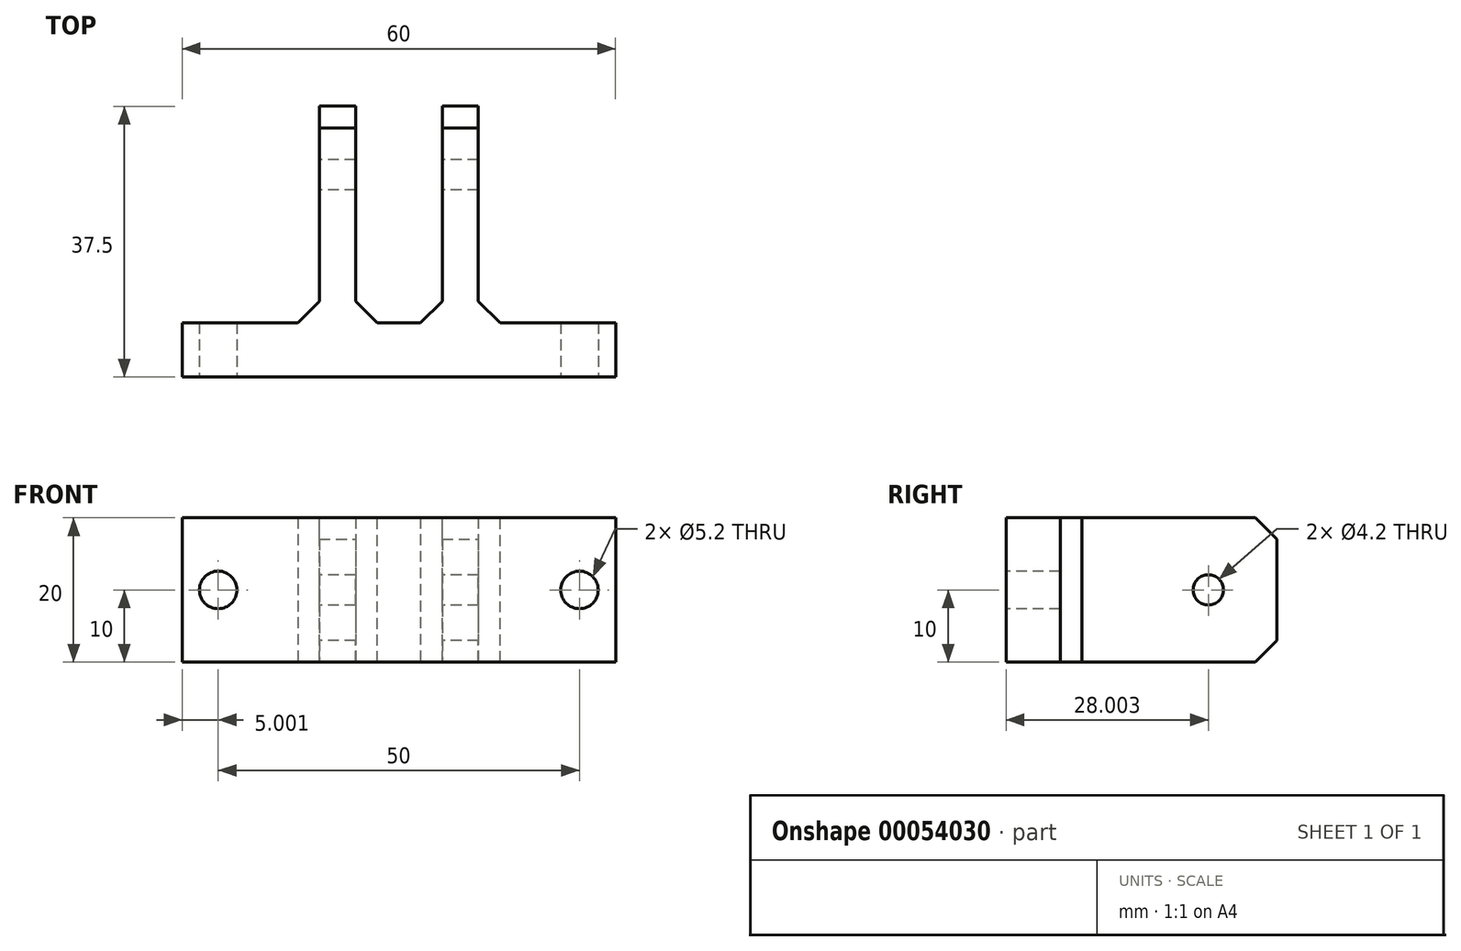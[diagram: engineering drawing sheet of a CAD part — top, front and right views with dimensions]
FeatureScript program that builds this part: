
annotation { "Feature Type Name" : "Feature", "Feature Type Description" : "" }
export const myFeature = defineFeature(function(context is Context, id is Id, definition is map)
    precondition{}
    {
        {
            var Q0;
            Q0=qCreatedBy(makeId("Top.planeOp"),FACE);
            var sketch = newSketch(context, id + "F0", { "sketchPlane" : qUnion([Q0])});
            skLineSegment(sketch, "E0.bottom", {"start": v(6.11, 32.08) * mm, "end": v(66.11, 32.08) * mm});
            skLineSegment(sketch, "E0.top", {"start": v(6.11, 39.58) * mm, "end": v(66.11, 39.58) * mm});
            skLineSegment(sketch, "E0.left", {"start": v(6.11, 32.08) * mm, "end": v(6.11, 39.58) * mm});
            skLineSegment(sketch, "E0.right", {"start": v(66.11, 32.08) * mm, "end": v(66.11, 39.58) * mm});
            skLineSegment(sketch, "E1.bottom", {"start": v(25.11, 39.58) * mm, "end": v(30.11, 39.58) * mm});
            skLineSegment(sketch, "E1.top", {"start": v(25.11, 69.58) * mm, "end": v(30.11, 69.58) * mm});
            skLineSegment(sketch, "E1.left", {"start": v(25.11, 39.58) * mm, "end": v(25.11, 69.58) * mm});
            skLineSegment(sketch, "E1.right", {"start": v(30.11, 39.58) * mm, "end": v(30.11, 69.58) * mm});
            skLineSegment(sketch, "E2.bottom", {"start": v(42.11, 69.58) * mm, "end": v(47.11, 69.58) * mm});
            skLineSegment(sketch, "E2.top", {"start": v(42.11, 39.58) * mm, "end": v(47.11, 39.58) * mm});
            skLineSegment(sketch, "E2.left", {"start": v(42.11, 69.58) * mm, "end": v(42.11, 39.58) * mm});
            skLineSegment(sketch, "E2.right", {"start": v(47.11, 69.58) * mm, "end": v(47.11, 39.58) * mm});
            skSolve(sketch);
        }
        {
            var Q0;
            Q0 = qSketchRegion(id + "F0", true);
            extrude(context, id + "F1", {"entities" : qUnion([Q0]), "depth" : 20 * mm});
        }
        {
            var Q0;
            Q0=makeQuery(id+"F1.opExtrude","SWEPT_FACE",FACE,{"disambiguationData":[OSD([sQuery(id+"F0.wireOp",EDGE,"E0.bottom")])]});
            var sketch = newSketch(context, id + "F2", { "sketchPlane" : qUnion([Q0])});
            skPoint(sketch, "E3", {"position": v(11.11, 10) * mm});
            skPoint(sketch, "E4", {"position": v(61.11, 10) * mm});
            skSolve(sketch);
        }
        {
            var Q0;
            Q0=sQuery(id+"F2.wireOp",VERTEX,"E3");
            var Q1;
            Q1=sQuery(id+"F2.wireOp",VERTEX,"E4");
            var Q2;
            Q2=makeQuery(id+"F1.opExtrude","SWEPT_BODY",BODY,{"disambiguationData":[OSD([sQuery(id+"F0.wireOp",EDGE,"E0.bottom"),sQuery(id+"F0.wireOp",EDGE,"E0.top"),sQuery(id+"F0.wireOp",EDGE,"E0.left"),sQuery(id+"F0.wireOp",EDGE,"E0.right"),sQuery(id+"F0.wireOp",EDGE,"E1.top"),sQuery(id+"F0.wireOp",EDGE,"E1.left"),sQuery(id+"F0.wireOp",EDGE,"E1.right"),sQuery(id+"F0.wireOp",EDGE,"E2.bottom"),sQuery(id+"F0.wireOp",EDGE,"E2.left"),sQuery(id+"F0.wireOp",EDGE,"E2.right")])]});
            hole(context, id + "F3", {"style" : HoleStyle.SIMPLE, "holeDiameter" : 5.2 * mm, "endStyle" : HoleEndStyle.THROUGH, "locations" : qUnion([Q0, Q1]), "scope" : qUnion([Q2])});
        }
        {
            var Q0;
            Q0=makeQuery(id+"F1.opExtrude","SWEPT_FACE",FACE,{"disambiguationData":[OSD([sQuery(id+"F0.wireOp",EDGE,"E1.left")])]});
            var sketch = newSketch(context, id + "F4", { "sketchPlane" : qUnion([Q0])});
            skPoint(sketch, "E5", {"position": v(-60.08, 10) * mm});
            skSolve(sketch);
        }
        {
            var Q0;
            Q0=sQuery(id+"F4.wireOp",VERTEX,"E5");
            var Q1;
            Q1=makeQuery(id+"F1.opExtrude","SWEPT_BODY",BODY,{"disambiguationData":[OSD([sQuery(id+"F0.wireOp",EDGE,"E0.bottom"),sQuery(id+"F0.wireOp",EDGE,"E0.top"),sQuery(id+"F0.wireOp",EDGE,"E0.left"),sQuery(id+"F0.wireOp",EDGE,"E0.right"),sQuery(id+"F0.wireOp",EDGE,"E1.top"),sQuery(id+"F0.wireOp",EDGE,"E1.left"),sQuery(id+"F0.wireOp",EDGE,"E1.right"),sQuery(id+"F0.wireOp",EDGE,"E2.bottom"),sQuery(id+"F0.wireOp",EDGE,"E2.left"),sQuery(id+"F0.wireOp",EDGE,"E2.right")])]});
            hole(context, id + "F5", {"style" : HoleStyle.SIMPLE, "holeDiameter" : 4.2 * mm, "endStyle" : HoleEndStyle.THROUGH, "locations" : qUnion([Q0]), "scope" : qUnion([Q1])});
        }
        {
            var Q0;
            Q0=makeQuery(id+"F1.opExtrude","CAP_EDGE",EDGE,{"disambiguationData":[OSD([sQuery(id+"F0.wireOp",EDGE,"E1.top")])],"isStart":false});
            var Q1;
            Q1=makeQuery(id+"F1.opExtrude","CAP_EDGE",EDGE,{"disambiguationData":[OSD([sQuery(id+"F0.wireOp",EDGE,"E2.bottom")])],"isStart":false});
            var Q2;
            Q2=makeQuery(id+"F1.opExtrude","CAP_EDGE",EDGE,{"disambiguationData":[OSD([sQuery(id+"F0.wireOp",EDGE,"E2.bottom")])],"isStart":true});
            var Q3;
            Q3=makeQuery(id+"F1.opExtrude","CAP_EDGE",EDGE,{"disambiguationData":[OSD([sQuery(id+"F0.wireOp",EDGE,"E1.top")])],"isStart":true});
            var Q4;
            Q4=makeQuery(id+"F1.opExtrude","SWEPT_EDGE",EDGE,{"disambiguationData":[OSD([sQuery(id+"F0.wireOp",EDGE,"E0.top"),sQuery(id+"F0.wireOp",EDGE,"E1.bottom"),sQuery(id+"F0.wireOp",EDGE,"E1.left")])]});
            var Q5;
            Q5=makeQuery(id+"F1.opExtrude","SWEPT_EDGE",EDGE,{"disambiguationData":[OSD([sQuery(id+"F0.wireOp",EDGE,"E0.top"),sQuery(id+"F0.wireOp",EDGE,"E2.top"),sQuery(id+"F0.wireOp",EDGE,"E2.right")])]});
            var Q6;
            Q6=makeQuery(id+"F1.opExtrude","SWEPT_EDGE",EDGE,{"disambiguationData":[OSD([sQuery(id+"F0.wireOp",EDGE,"E0.top"),sQuery(id+"F0.wireOp",EDGE,"E2.top"),sQuery(id+"F0.wireOp",EDGE,"E2.left")])]});
            var Q7;
            Q7=makeQuery(id+"F1.opExtrude","SWEPT_EDGE",EDGE,{"disambiguationData":[OSD([sQuery(id+"F0.wireOp",EDGE,"E0.top"),sQuery(id+"F0.wireOp",EDGE,"E1.bottom"),sQuery(id+"F0.wireOp",EDGE,"E1.right")])]});
            chamfer(context, id + "F6", {"entities" : qUnion([Q0, Q1, Q2, Q3, Q4, Q5, Q6, Q7]), "width" : 3 * mm, "tangentPropagation" : true});
        }
    });
